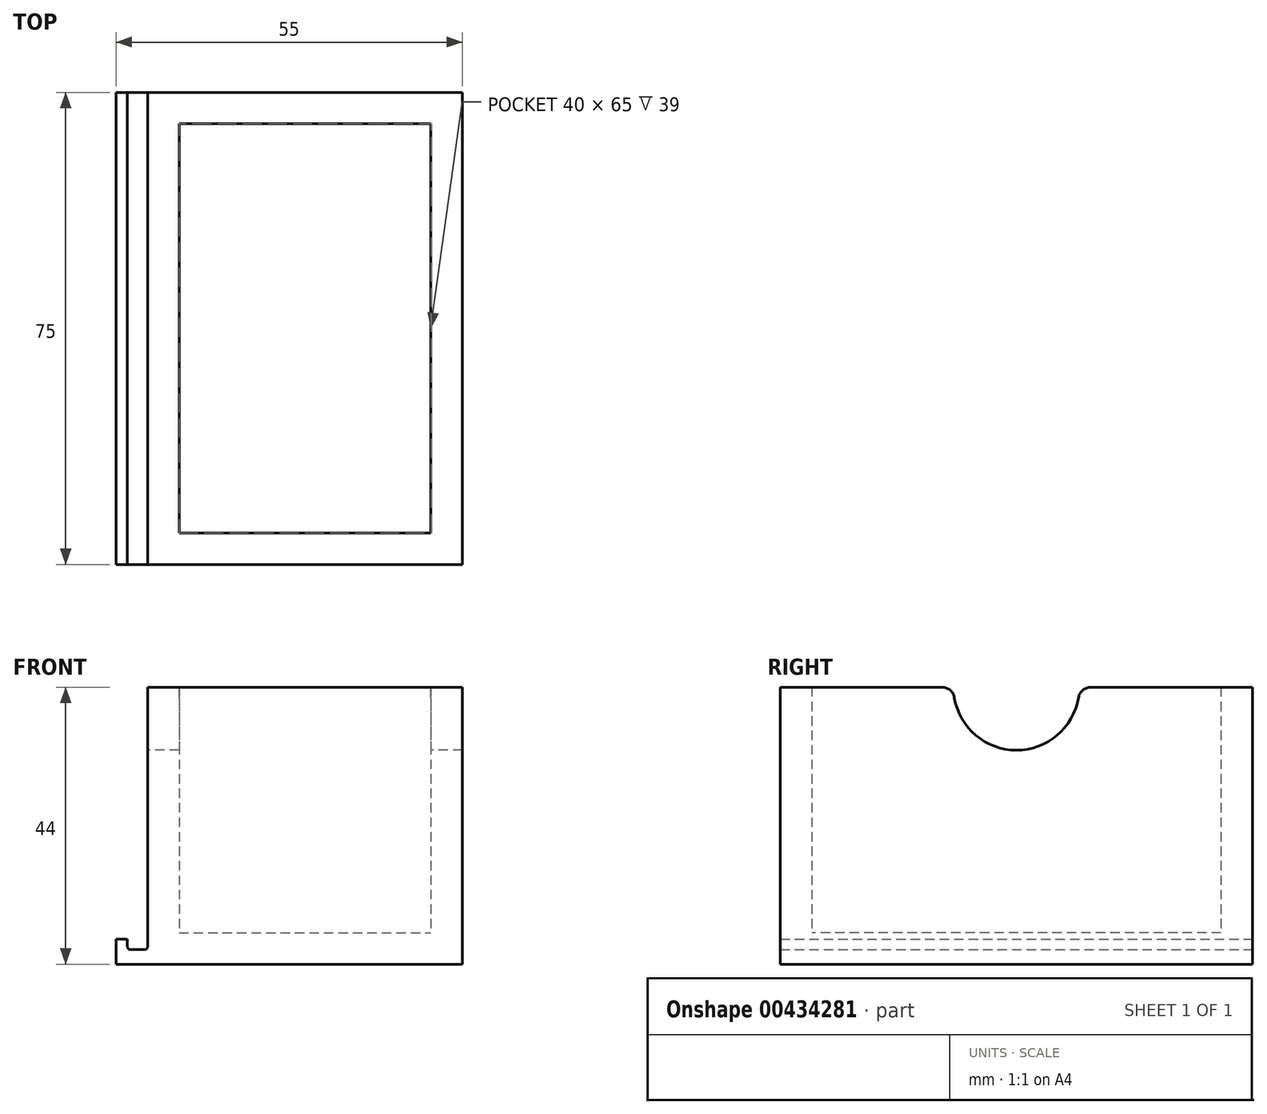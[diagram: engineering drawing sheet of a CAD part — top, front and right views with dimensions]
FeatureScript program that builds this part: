
annotation { "Feature Type Name" : "Feature", "Feature Type Description" : "" }
export const myFeature = defineFeature(function(context is Context, id is Id, definition is map)
    precondition{}
    {
        {
            var Q0;
            Q0=qCreatedBy(makeId("Front.planeOp"),FACE);
            var sketch = newSketch(context, id + "F0", { "sketchPlane" : qUnion([Q0])});
            skLineSegment(sketch, "E0.bottom", {"start": v(-25, 4) * mm, "end": v(25, 4) * mm});
            skLineSegment(sketch, "E0.top", {"start": v(-25, 0) * mm, "end": v(25, 0) * mm});
            skLineSegment(sketch, "E0.left", {"start": v(-25, 4) * mm, "end": v(-25, 0) * mm});
            skLineSegment(sketch, "E0.right", {"start": v(25, 4) * mm, "end": v(25, 0) * mm});
            skPoint(sketch, "E0.middle", {"position": v(0, 2) * mm});
            skLineSegment(sketch, "E1.bottom", {"start": v(-25, 0) * mm, "end": v(-30, 0) * mm});
            skLineSegment(sketch, "E1.top", {"start": v(-28.2, 4) * mm, "end": v(-30, 4) * mm});
            skLineSegment(sketch, "E1.right", {"start": v(-30, 0) * mm, "end": v(-30, 4) * mm});
            skLineSegment(sketch, "E2.top", {"start": v(-28.2, 2.3) * mm, "end": v(-25, 2.3) * mm});
            skLineSegment(sketch, "E2.left", {"start": v(-28.2, 4) * mm, "end": v(-28.2, 2.3) * mm});
            skLineSegment(sketch, "E3", {"start": v(-25, 2.3) * mm, "end": v(-25, 0) * mm});
            skSolve(sketch);
        }
        {
            var Q0;
            Q0 = qSketchRegion(id + "F0", true);
            extrude(context, id + "F1", {"entities" : qUnion([Q0]), "depth" : 75 * mm});
        }
        {
            var Q0;
            Q0=makeQuery(id+"F1.opExtrude","SWEPT_EDGE",EDGE,{"disambiguationData":[OSD([sQuery(id+"F0.wireOp",EDGE,"E0.left"),sQuery(id+"F0.wireOp",EDGE,"E2.top"),sQuery(id+"F0.wireOp",EDGE,"E3")])]});
            var Q1;
            Q1=makeQuery(id+"F1.opExtrude","SWEPT_EDGE",EDGE,{"disambiguationData":[OSD([sQuery(id+"F0.wireOp",EDGE,"E2.top"),sQuery(id+"F0.wireOp",EDGE,"E2.left")])]});
            fillet(context, id + "F2", {"entities" : qUnion([Q0, Q1]), "radius" : 0.5 * mm, "tangentPropagation" : true, "allowEdgeOverflow" : false});
        }
        {
            var Q0;
            Q0=qCreatedBy(makeId("Front.planeOp"),FACE);
            var sketch = newSketch(context, id + "F3", { "sketchPlane" : qUnion([Q0])});
            skLineSegment(sketch, "E4.bottom", {"start": v(-25, 4) * mm, "end": v(25, 4) * mm});
            skLineSegment(sketch, "E4.top", {"start": v(-25, 44) * mm, "end": v(25, 44) * mm});
            skLineSegment(sketch, "E4.left", {"start": v(-25, 4) * mm, "end": v(-25, 44) * mm});
            skLineSegment(sketch, "E4.right", {"start": v(25, 4) * mm, "end": v(25, 44) * mm});
            skSolve(sketch);
        }
        {
            var Q0;
            Q0 = qSketchRegion(id + "F3", true);
            extrude(context, id + "F4", {"entities" : qUnion([Q0]), "operationType" : NewBodyOperationType.ADD, "depth" : 75 * mm});
        }
        {
            var Q0;
            Q0=makeQuery(id+"F4.opExtrude","SWEPT_FACE",FACE,{"disambiguationData":[OSD([sQuery(id+"F3.wireOp",EDGE,"E4.top")])]});
            shell(context, id + "F5", {"entities" : qUnion([Q0]), "thickness" : 5 * mm});
        }
        {
            var Q0;
            Q0=makeQuery(id+"F4.boolean.opBoolean","MERGE",FACE,{"derivedFrom":[makeQuery(id+"F1.opExtrude","SWEPT_FACE",FACE,{"disambiguationData":[OSD([sQuery(id+"F0.wireOp",EDGE,"E0.left")])]}),makeQuery(id+"F4.opExtrude","SWEPT_FACE",FACE,{"disambiguationData":[OSD([sQuery(id+"F3.wireOp",EDGE,"E4.left")])]})]});
            var sketch = newSketch(context, id + "F6", { "sketchPlane" : qUnion([Q0])});
            skCircle(sketch, "E5", {"center": v(37.5, 44) * mm, "radius": 10 * mm});
            skSolve(sketch);
        }
        {
            var Q0;
            Q0 = qSketchRegion(id + "F6", true);
            var Q1;
            Q1=makeQuery(id+"F4.boolean.opBoolean","MERGE",FACE,{"derivedFrom":[makeQuery(id+"F1.opExtrude","SWEPT_FACE",FACE,{"disambiguationData":[OSD([sQuery(id+"F0.wireOp",EDGE,"E0.right")])]}),makeQuery(id+"F4.opExtrude","SWEPT_FACE",FACE,{"disambiguationData":[OSD([sQuery(id+"F3.wireOp",EDGE,"E4.right")])]})]});
            extrude(context, id + "F7", {"entities" : qUnion([Q0]), "operationType" : NewBodyOperationType.REMOVE, "endBound" : BoundingType.UP_TO_SURFACE, "oppositeDirection" : true, "endBoundEntityFace" : qUnion([Q1]), "depth" : 25 * mm});
        }
        {
            var Q0;
            Q0=makeQuery(id+"F7.boolean.opBoolean","INTERSECT",EDGE,{"disambiguationData":[OD(0.0)],"derivedFrom":[makeQuery(id+"F4.opExtrude","SWEPT_FACE",FACE,{"disambiguationData":[OSD([sQuery(id+"F3.wireOp",EDGE,"E4.top")])]}),makeQuery(id+"F7.opExtrude","SWEPT_FACE",FACE,{"disambiguationData":[OSD([sQuery(id+"F6.wireOp",EDGE,"E5")])]})]});
            var Q1;
            Q1=makeQuery(id+"F7.boolean.opBoolean","INTERSECT",EDGE,{"disambiguationData":[OD(2.0)],"derivedFrom":[makeQuery(id+"F4.opExtrude","SWEPT_FACE",FACE,{"disambiguationData":[OSD([sQuery(id+"F3.wireOp",EDGE,"E4.top")])]}),makeQuery(id+"F7.opExtrude","SWEPT_FACE",FACE,{"disambiguationData":[OSD([sQuery(id+"F6.wireOp",EDGE,"E5")])]})]});
            var Q2;
            Q2=makeQuery(id+"F7.boolean.opBoolean","INTERSECT",EDGE,{"disambiguationData":[OD(1.0)],"derivedFrom":[makeQuery(id+"F4.opExtrude","SWEPT_FACE",FACE,{"disambiguationData":[OSD([sQuery(id+"F3.wireOp",EDGE,"E4.top")])]}),makeQuery(id+"F7.opExtrude","SWEPT_FACE",FACE,{"disambiguationData":[OSD([sQuery(id+"F6.wireOp",EDGE,"E5")])]})]});
            var Q3;
            Q3=makeQuery(id+"F7.boolean.opBoolean","INTERSECT",EDGE,{"disambiguationData":[OD(3.0)],"derivedFrom":[makeQuery(id+"F4.opExtrude","SWEPT_FACE",FACE,{"disambiguationData":[OSD([sQuery(id+"F3.wireOp",EDGE,"E4.top")])]}),makeQuery(id+"F7.opExtrude","SWEPT_FACE",FACE,{"disambiguationData":[OSD([sQuery(id+"F6.wireOp",EDGE,"E5")])]})]});
            fillet(context, id + "F8", {"entities" : qUnion([Q0, Q1, Q2, Q3]), "radius" : 2 * mm, "tangentPropagation" : true, "allowEdgeOverflow" : false});
        }
    });
